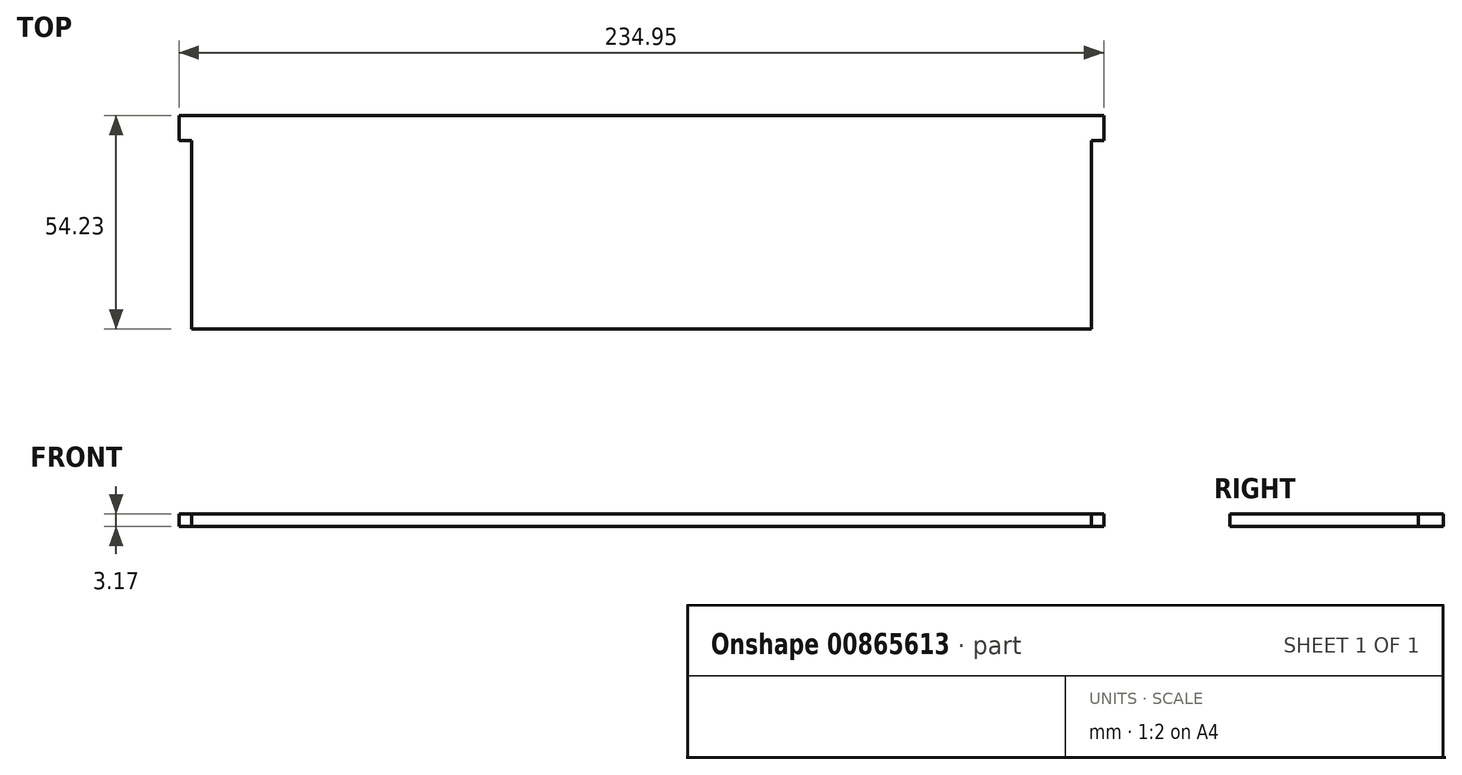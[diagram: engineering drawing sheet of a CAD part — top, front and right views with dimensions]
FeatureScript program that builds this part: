
annotation { "Feature Type Name" : "Feature", "Feature Type Description" : "" }
export const myFeature = defineFeature(function(context is Context, id is Id, definition is map)
    precondition{}
    {
        {
            var Q0;
            Q0=qCreatedBy(makeId("Top.planeOp"),FACE);
            var sketch = newSketch(context, id + "F0", { "sketchPlane" : qUnion([Q0])});
            skLineSegment(sketch, "E0.bottom", {"start": v(0, 0) * mm, "end": v(228.6, 0) * mm});
            skLineSegment(sketch, "E0.top", {"start": v(0, -54.23) * mm, "end": v(228.6, -54.23) * mm});
            skLineSegment(sketch, "E0.left", {"start": v(0, 0) * mm, "end": v(0, -54.23) * mm});
            skLineSegment(sketch, "E0.right", {"start": v(228.6, 0) * mm, "end": v(228.6, -54.23) * mm});
            skLineSegment(sketch, "E1.bottom", {"start": v(228.6, 0) * mm, "end": v(231.78, 0) * mm});
            skLineSegment(sketch, "E1.top", {"start": v(228.6, -6.35) * mm, "end": v(231.78, -6.35) * mm});
            skLineSegment(sketch, "E1.left", {"start": v(228.6, 0) * mm, "end": v(228.6, -6.35) * mm});
            skLineSegment(sketch, "E1.right", {"start": v(231.78, 0) * mm, "end": v(231.78, -6.35) * mm});
            skLineSegment(sketch, "E2.bottom", {"start": v(0, 0) * mm, "end": v(-3.18, 0) * mm});
            skLineSegment(sketch, "E2.top", {"start": v(0, -6.35) * mm, "end": v(-3.17, -6.35) * mm});
            skLineSegment(sketch, "E2.left", {"start": v(0, 0) * mm, "end": v(0, -6.35) * mm});
            skLineSegment(sketch, "E2.right", {"start": v(-3.18, 0) * mm, "end": v(-3.17, -6.35) * mm});
            skSolve(sketch);
        }
        {
            var Q0;
            Q0=makeQuery(id+"F0.imprint","IMPRINT",FACE,{"disambiguationData":[TD([[makeQuery(id+"F0.imprint","IMPRINT",EDGE,{"derivedFrom":sQuery(id+"F0.wireOp",EDGE,"E0.bottom")}),-1.0]])]});
            var Q1;
            Q1=makeQuery(id+"F0.imprint","IMPRINT",FACE,{"disambiguationData":[TD([[makeQuery(id+"F0.imprint","IMPRINT",EDGE,{"derivedFrom":sQuery(id+"F0.wireOp",EDGE,"E2.bottom")}),1.0]])]});
            var Q2;
            Q2=makeQuery(id+"F0.imprint","IMPRINT",FACE,{"disambiguationData":[TD([[makeQuery(id+"F0.imprint","IMPRINT",EDGE,{"derivedFrom":sQuery(id+"F0.wireOp",EDGE,"E1.bottom")}),-1.0]])]});
            extrude(context, id + "F1", {"entities" : qUnion([Q0, Q1, Q2]), "depth" : 3.17 * mm, "offsetDistance" : 25.4 * mm});
        }
    });
